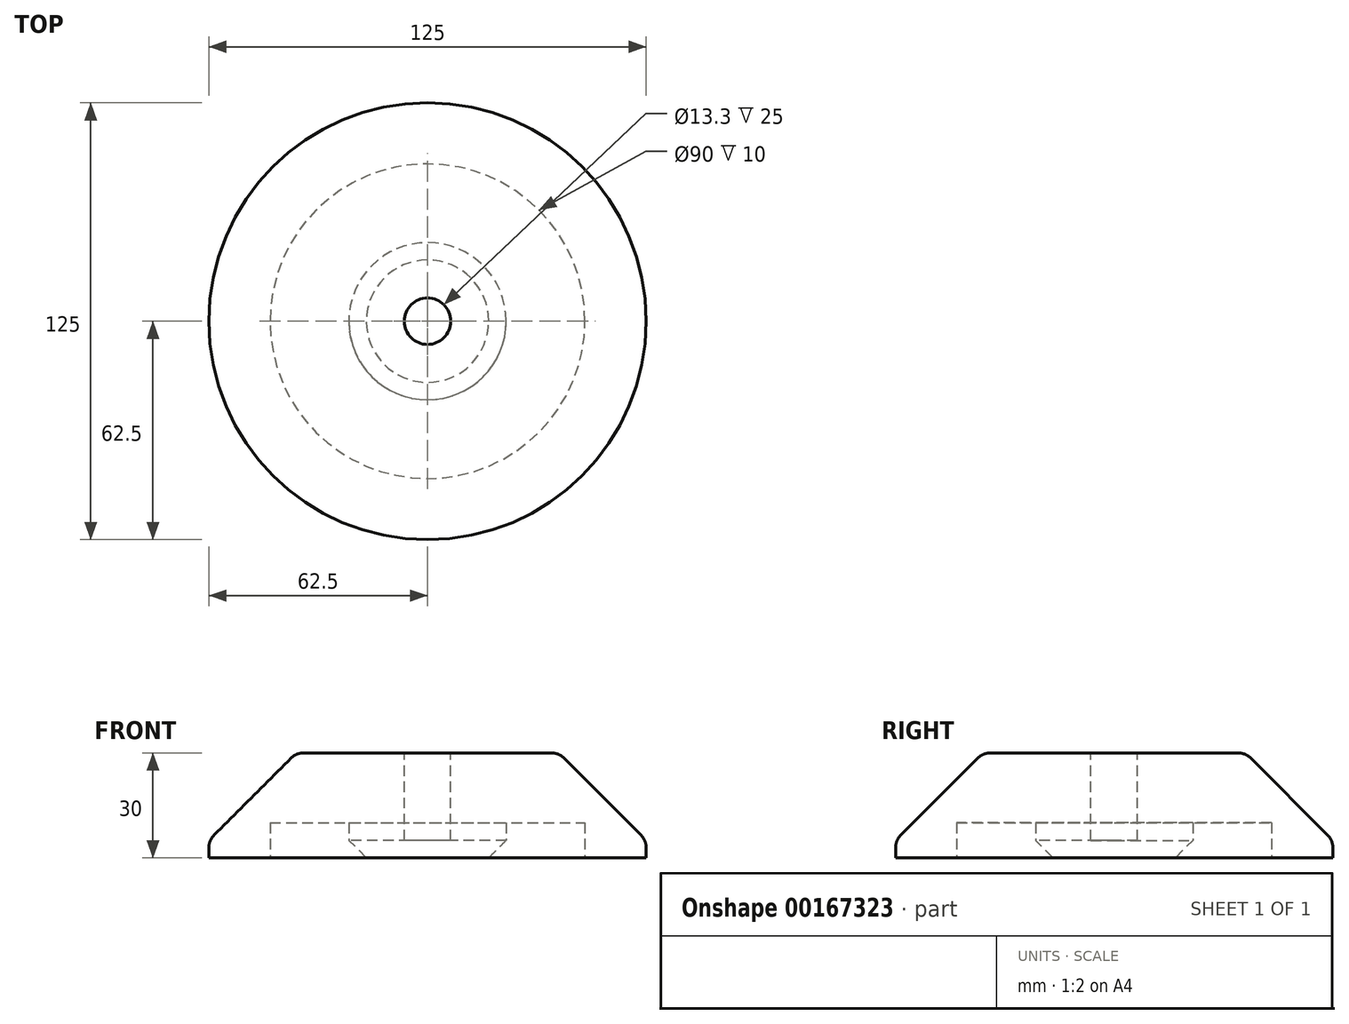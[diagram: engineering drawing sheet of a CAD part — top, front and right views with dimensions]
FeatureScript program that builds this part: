
annotation { "Feature Type Name" : "Feature", "Feature Type Description" : "" }
export const myFeature = defineFeature(function(context is Context, id is Id, definition is map)
    precondition{}
    {
        {
            var Q0;
            Q0=qCreatedBy(makeId("Top.planeOp"),FACE);
            var sketch = newSketch(context, id + "F0", { "sketchPlane" : qUnion([Q0])});
            skCircle(sketch, "E0", {"center": v(0, 0) * mm, "radius": 62.5 * mm});
            skSolve(sketch);
        }
        {
            var Q0;
            Q0=makeQuery(id+"F0.imprint","IMPRINT",FACE,{"disambiguationData":[TD([[makeQuery(id+"F0.imprint","IMPRINT",EDGE,{"derivedFrom":sQuery(id+"F0.wireOp",EDGE,"E0")}),1.0]])]});
            extrude(context, id + "F1", {"entities" : qUnion([Q0]), "depth" : 30 * mm});
        }
        {
            var Q0;
            Q0=makeQuery(id+"F1.opExtrude","CAP_EDGE",EDGE,{"disambiguationData":[OSD([sQuery(id+"F0.wireOp",EDGE,"E0")])],"isStart":false});
            chamfer(context, id + "F2", {"entities" : qUnion([Q0]), "width" : 25 * mm, "tangentPropagation" : true});
        }
        {
            var Q0;
            Q0=makeQuery(id+"F1.opExtrude","CAP_FACE",FACE,{"disambiguationData":[OSD([sQuery(id+"F0.wireOp",EDGE,"E0")])],"isStart":false});
            var sketch = newSketch(context, id + "F3", { "sketchPlane" : qUnion([Q0])});
            skCircle(sketch, "E1", {"center": v(0, 0) * mm, "radius": 6.65 * mm});
            skSolve(sketch);
        }
        {
            var Q0;
            Q0=makeQuery(id+"F3.imprint","IMPRINT",FACE,{"disambiguationData":[TD([[makeQuery(id+"F3.imprint","IMPRINT",EDGE,{"derivedFrom":sQuery(id+"F3.wireOp",EDGE,"E1")}),1.0]])]});
            extrude(context, id + "F4", {"entities" : qUnion([Q0]), "operationType" : NewBodyOperationType.REMOVE, "oppositeDirection" : true, "depth" : 25 * mm});
        }
        {
            var Q0;
            {var subQ0=sQuery(id+"F0.wireOp",EDGE,"E0");Q0=makeQuery(id+"F2.opChamfer","BLEND_EDGE",EDGE,{"blendedFrom":[makeQuery(id+"F1.opExtrude","CAP_EDGE",EDGE,{"disambiguationData":[OSD([subQ0])],"isStart":false}),makeQuery(id+"F1.opExtrude","CAP_FACE",FACE,{"disambiguationData":[OSD([subQ0])],"isStart":false})],"blendedInto":[makeQuery(id+"F1.opExtrude","CAP_FACE",FACE,{"disambiguationData":[OSD([subQ0])],"isStart":false})]});}
            fillet(context, id + "F5", {"entities" : qUnion([Q0]), "radius" : 5 * mm, "tangentPropagation" : true, "allowEdgeOverflow" : false});
        }
        {
            var Q0;
            {var subQ0=sQuery(id+"F0.wireOp",EDGE,"E0");Q0=makeQuery(id+"F2.opChamfer","BLEND_EDGE",EDGE,{"blendedFrom":[makeQuery(id+"F1.opExtrude","CAP_EDGE",EDGE,{"disambiguationData":[OSD([subQ0])],"isStart":false}),makeQuery(id+"F1.opExtrude","SWEPT_FACE",FACE,{"disambiguationData":[OSD([subQ0])]})],"blendedInto":[makeQuery(id+"F1.opExtrude","SWEPT_FACE",FACE,{"disambiguationData":[OSD([subQ0])]})]});}
            fillet(context, id + "F6", {"entities" : qUnion([Q0]), "radius" : 5 * mm, "tangentPropagation" : true, "allowEdgeOverflow" : false});
        }
        {
            var Q0;
            Q0=makeQuery(id+"F1.opExtrude","CAP_FACE",FACE,{"disambiguationData":[OSD([sQuery(id+"F0.wireOp",EDGE,"E0")])],"isStart":true});
            var sketch = newSketch(context, id + "F7", { "sketchPlane" : qUnion([Q0])});
            skCircle(sketch, "E2", {"center": v(0, 0) * mm, "radius": 22.5 * mm});
            skCircle(sketch, "E3", {"center": v(0, 0) * mm, "radius": 45 * mm});
            skSolve(sketch);
        }
        {
            var Q0;
            Q0 = qSketchRegion(id + "F7", true);
            extrude(context, id + "F8", {"entities" : qUnion([Q0]), "operationType" : NewBodyOperationType.REMOVE, "oppositeDirection" : true, "depth" : 10 * mm});
        }
        {
            var Q0;
            Q0=makeQuery(id+"F8.boolean.opBoolean","COPY",EDGE,{"derivedFrom":makeQuery(id+"F8.opExtrude","CAP_EDGE",EDGE,{"disambiguationData":[OSD([sQuery(id+"F7.wireOp",EDGE,"E3")])],"isStart":true})});
            var Q1;
            Q1=makeQuery(id+"F8.boolean.opBoolean","COPY",EDGE,{"derivedFrom":makeQuery(id+"F8.opExtrude","CAP_EDGE",EDGE,{"disambiguationData":[OSD([sQuery(id+"F7.wireOp",EDGE,"E2")])],"isStart":true})});
            chamfer(context, id + "F9", {"entities" : qUnion([Q0, Q1]), "width" : 5 * mm, "tangentPropagation" : true});
        }
    });
